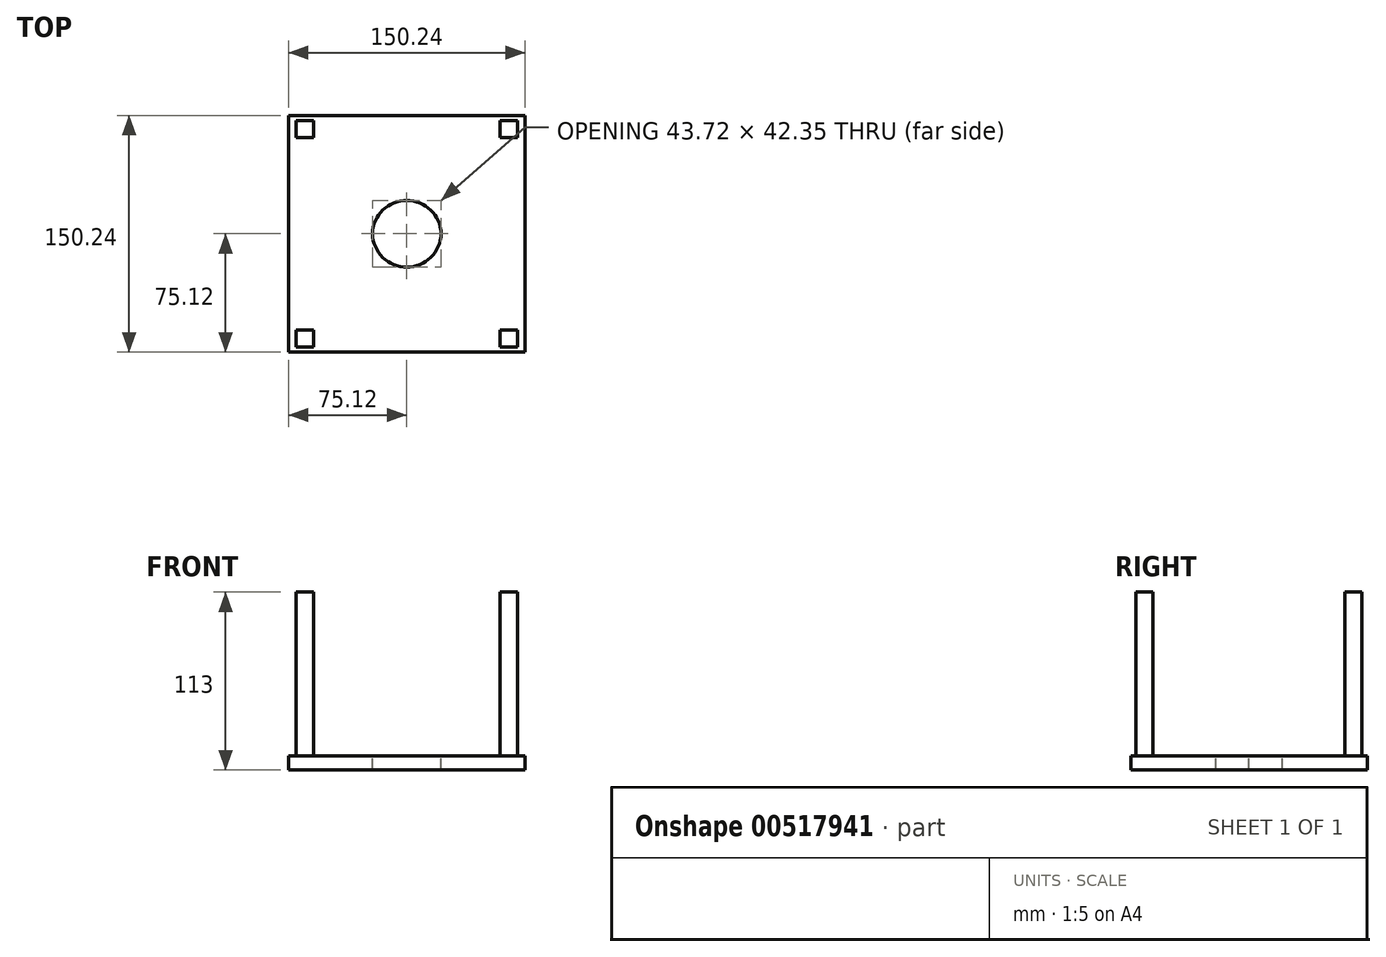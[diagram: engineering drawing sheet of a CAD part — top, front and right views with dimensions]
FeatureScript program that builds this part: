
annotation { "Feature Type Name" : "Feature", "Feature Type Description" : "" }
export const myFeature = defineFeature(function(context is Context, id is Id, definition is map)
    precondition{}
    {
        {
            var Q0;
            Q0=qCreatedBy(makeId("Top.planeOp"),FACE);
            var sketch = newSketch(context, id + "F0", { "sketchPlane" : qUnion([Q0])});
            skLineSegment(sketch, "E0.bottom", {"start": v(-70.38, -61) * mm, "end": v(-59.12, -61) * mm});
            skLineSegment(sketch, "E0.top", {"start": v(-70.38, -71.78) * mm, "end": v(-59.12, -71.78) * mm});
            skLineSegment(sketch, "E0.left", {"start": v(-70.38, -61) * mm, "end": v(-70.38, -71.78) * mm});
            skLineSegment(sketch, "E0.right", {"start": v(-59.12, -61) * mm, "end": v(-59.12, -71.78) * mm});
            skSolve(sketch);
        }
        {
            var Q0;
            Q0=makeQuery(id+"F0.imprint","IMPRINT",FACE,{"disambiguationData":[TD([[makeQuery(id+"F0.imprint","IMPRINT",EDGE,{"derivedFrom":sQuery(id+"F0.wireOp",EDGE,"E0.bottom")}),-1.0]])]});
            extrude(context, id + "F1", {"entities" : qUnion([Q0]), "depth" : 104 * mm, "offsetDistance" : 25 * mm});
        }
        {
            var Q0;
            Q0=qCreatedBy(makeId("Top.planeOp"),FACE);
            var sketch = newSketch(context, id + "F2", { "sketchPlane" : qUnion([Q0])});
            skLineSegment(sketch, "E1.bottom", {"start": v(-75.12, -75.12) * mm, "end": v(74.2, -75.12) * mm});
            skLineSegment(sketch, "E1.top", {"start": v(-75.12, 74.81) * mm, "end": v(74.2, 74.81) * mm});
            skLineSegment(sketch, "E1.left", {"start": v(-75.12, -75.12) * mm, "end": v(-75.12, 74.81) * mm});
            skLineSegment(sketch, "E1.right", {"start": v(74.2, -75.12) * mm, "end": v(74.2, 74.81) * mm});
            skSolve(sketch);
        }
        {
            var Q0;
            Q0=makeQuery(id+"F2.imprint","IMPRINT",FACE,{"disambiguationData":[TD([[makeQuery(id+"F2.imprint","IMPRINT",EDGE,{"derivedFrom":sQuery(id+"F2.wireOp",EDGE,"E1.bottom")}),1.0]])]});
            extrude(context, id + "F3", {"entities" : qUnion([Q0]), "operationType" : NewBodyOperationType.ADD, "oppositeDirection" : true, "depth" : 9 * mm, "offsetDistance" : 25 * mm});
        }
        {
            var Q0;
            Q0=makeQuery(id+"F3.opExtrude","CAP_FACE",FACE,{"disambiguationData":[OSD([sQuery(id+"F2.wireOp",EDGE,"E1.bottom"),sQuery(id+"F2.wireOp",EDGE,"E1.top"),sQuery(id+"F2.wireOp",EDGE,"E1.left"),sQuery(id+"F2.wireOp",EDGE,"E1.right")])],"isStart":true});
            var sketch = newSketch(context, id + "F4", { "sketchPlane" : qUnion([Q0])});
            skCircle(sketch, "E2", {"center": v(0, 0.7) * mm, "radius": 21.87 * mm});
            skSolve(sketch);
        }
        {
            var Q0;
            Q0=makeQuery(id+"F4.imprint","IMPRINT",FACE,{"disambiguationData":[TD([[makeQuery(id+"F4.imprint","IMPRINT",EDGE,{"derivedFrom":sQuery(id+"F4.wireOp",EDGE,"E2")}),1.0]])]});
            extrude(context, id + "F5", {"entities" : qUnion([Q0]), "operationType" : NewBodyOperationType.REMOVE, "endBound" : BoundingType.THROUGH_ALL, "oppositeDirection" : true, "depth" : 68 * mm, "offsetDistance" : 25 * mm});
        }
        {
            var Q0;
            Q0=makeQuery(id+"F1.opExtrude","SWEPT_BODY",BODY,{"disambiguationData":[OSD([sQuery(id+"F0.wireOp",EDGE,"E0.bottom"),sQuery(id+"F0.wireOp",EDGE,"E0.top"),sQuery(id+"F0.wireOp",EDGE,"E0.left"),sQuery(id+"F0.wireOp",EDGE,"E0.right")])]});
            var Q1;
            Q1=qCreatedBy(makeId("Front.planeOp"),FACE);
            mirror(context, id + "F6", {"operationType" : NewBodyOperationType.ADD, "entities" : qUnion([Q0]), "mirrorPlane" : qUnion([Q1])});
        }
        {
            var Q0;
            Q0=makeQuery(id+"F1.opExtrude","SWEPT_BODY",BODY,{"disambiguationData":[OSD([sQuery(id+"F0.wireOp",EDGE,"E0.bottom"),sQuery(id+"F0.wireOp",EDGE,"E0.top"),sQuery(id+"F0.wireOp",EDGE,"E0.left"),sQuery(id+"F0.wireOp",EDGE,"E0.right")])]});
            var Q1;
            Q1=qCreatedBy(makeId("Right.planeOp"),FACE);
            mirror(context, id + "F7", {"operationType" : NewBodyOperationType.ADD, "entities" : qUnion([Q0]), "mirrorPlane" : qUnion([Q1])});
        }
    });
